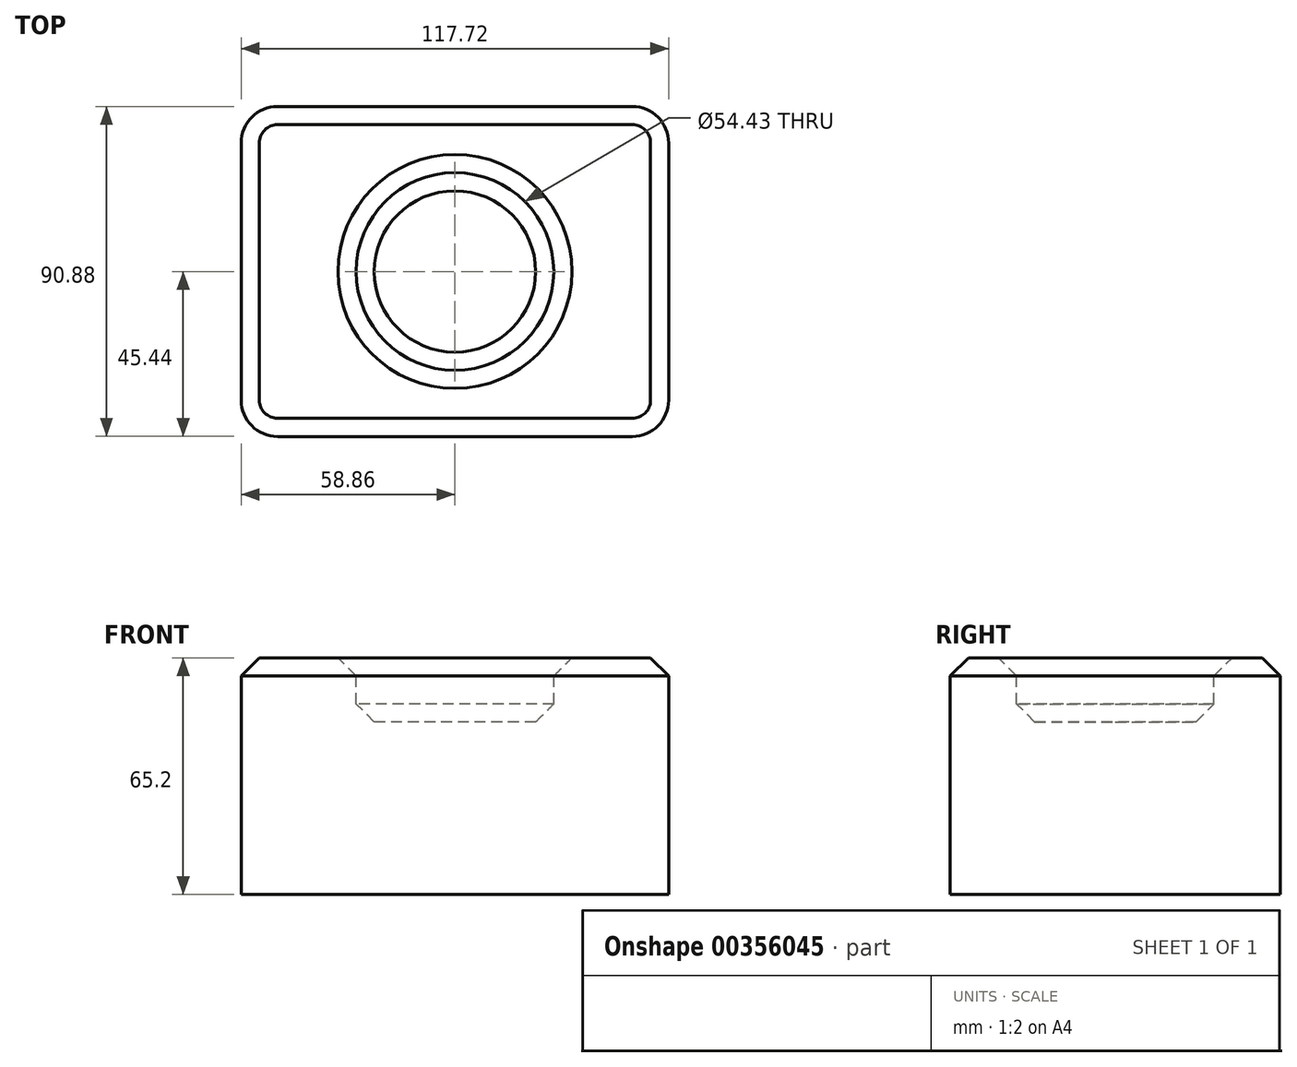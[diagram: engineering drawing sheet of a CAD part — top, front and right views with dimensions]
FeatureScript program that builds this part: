
annotation { "Feature Type Name" : "Feature", "Feature Type Description" : "" }
export const myFeature = defineFeature(function(context is Context, id is Id, definition is map)
    precondition{}
    {
        {
            var Q0;
            Q0=qCreatedBy(makeId("Top.planeOp"),FACE);
            var sketch = newSketch(context, id + "F0", { "sketchPlane" : qUnion([Q0])});
            skLineSegment(sketch, "E0.bottom", {"start": v(-58.86, -45.44) * mm, "end": v(58.86, -45.44) * mm});
            skLineSegment(sketch, "E0.top", {"start": v(-58.86, 45.44) * mm, "end": v(58.86, 45.44) * mm});
            skLineSegment(sketch, "E0.left", {"start": v(-58.86, -45.44) * mm, "end": v(-58.86, 45.44) * mm});
            skLineSegment(sketch, "E0.right", {"start": v(58.86, -45.44) * mm, "end": v(58.86, 45.44) * mm});
            skPoint(sketch, "E0.middle", {"position": v(0, 0) * mm});
            skSolve(sketch);
        }
        {
            var Q0;
            Q0=makeQuery(id+"F0.imprint","IMPRINT",FACE,{"disambiguationData":[TD([[makeQuery(id+"F0.imprint","IMPRINT",EDGE,{"derivedFrom":sQuery(id+"F0.wireOp",EDGE,"E0.bottom")}),1.0]])]});
            extrude(context, id + "F1", {"entities" : qUnion([Q0]), "depth" : 65.2 * mm});
        }
        {
            var Q0;
            Q0=makeQuery(id+"F1.opExtrude","SWEPT_EDGE",EDGE,{"disambiguationData":[OSD([sQuery(id+"F0.wireOp",EDGE,"E0.top"),sQuery(id+"F0.wireOp",EDGE,"E0.left")])]});
            var Q1;
            Q1=makeQuery(id+"F1.opExtrude","SWEPT_EDGE",EDGE,{"disambiguationData":[OSD([sQuery(id+"F0.wireOp",EDGE,"E0.bottom"),sQuery(id+"F0.wireOp",EDGE,"E0.left")])]});
            var Q2;
            Q2=makeQuery(id+"F1.opExtrude","SWEPT_EDGE",EDGE,{"disambiguationData":[OSD([sQuery(id+"F0.wireOp",EDGE,"E0.bottom"),sQuery(id+"F0.wireOp",EDGE,"E0.right")])]});
            var Q3;
            Q3=makeQuery(id+"F1.opExtrude","SWEPT_EDGE",EDGE,{"disambiguationData":[OSD([sQuery(id+"F0.wireOp",EDGE,"E0.top"),sQuery(id+"F0.wireOp",EDGE,"E0.right")])]});
            fillet(context, id + "F2", {"entities" : qUnion([Q0, Q1, Q2, Q3]), "radius" : 10 * mm, "tangentPropagation" : true, "allowEdgeOverflow" : false});
        }
        {
            var Q0;
            Q0=makeQuery(id+"F1.opExtrude","CAP_FACE",FACE,{"disambiguationData":[OSD([sQuery(id+"F0.wireOp",EDGE,"E0.bottom"),sQuery(id+"F0.wireOp",EDGE,"E0.top"),sQuery(id+"F0.wireOp",EDGE,"E0.left"),sQuery(id+"F0.wireOp",EDGE,"E0.right")])],"isStart":false});
            chamfer(context, id + "F3", {"entities" : qUnion([Q0]), "width" : 5 * mm, "tangentPropagation" : true});
        }
        {
            var Q0;
            Q0=makeQuery(id+"F1.opExtrude","CAP_FACE",FACE,{"disambiguationData":[OSD([sQuery(id+"F0.wireOp",EDGE,"E0.bottom"),sQuery(id+"F0.wireOp",EDGE,"E0.top"),sQuery(id+"F0.wireOp",EDGE,"E0.left"),sQuery(id+"F0.wireOp",EDGE,"E0.right")])],"isStart":false});
            var sketch = newSketch(context, id + "F4", { "sketchPlane" : qUnion([Q0])});
            skCircle(sketch, "E1", {"center": v(0, 0) * mm, "radius": 27.22 * mm});
            skSolve(sketch);
        }
        {
            var Q0;
            Q0=makeQuery(id+"F4.imprint","IMPRINT",FACE,{"disambiguationData":[TD([[makeQuery(id+"F4.imprint","IMPRINT",EDGE,{"derivedFrom":sQuery(id+"F4.wireOp",EDGE,"E1")}),1.0]])]});
            extrude(context, id + "F5", {"entities" : qUnion([Q0]), "operationType" : NewBodyOperationType.REMOVE, "oppositeDirection" : true, "depth" : 17.7 * mm});
        }
        {
            var Q0;
            Q0=makeQuery(id+"F5.boolean.opBoolean","COPY",FACE,{"derivedFrom":makeQuery(id+"F5.opExtrude","SWEPT_FACE",FACE,{"disambiguationData":[OSD([sQuery(id+"F4.wireOp",EDGE,"E1")])]})});
            var Q1;
            Q1=makeQuery(id+"F5.boolean.opBoolean","COPY",FACE,{"derivedFrom":makeQuery(id+"F5.opExtrude","CAP_FACE",FACE,{"disambiguationData":[OSD([sQuery(id+"F4.wireOp",EDGE,"E1")])],"isStart":false})});
            chamfer(context, id + "F6", {"entities" : qUnion([Q0, Q1]), "width" : 5 * mm, "tangentPropagation" : true});
        }
    });
